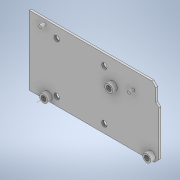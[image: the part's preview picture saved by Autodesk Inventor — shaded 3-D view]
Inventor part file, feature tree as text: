
AUTODESK INVENTOR PART (.ipt)
format: ipt  version: 2021 (Build 250183000, 183)  size: 338,944 bytes
history: native  units: mm
features: reference x23, other x6, sketch x5, plane x2, extrude x2, chamfer x1
ambient origin geometry x8: Origin, YZ Plane, XZ Plane, XY Plane, X Axis, Y Axis, Z Axis, Center Point
bodies: Volumenkörper1 (feature_tree)
feature tree (39):
  plane  "Arbeitsebene1"
  extrude  "Extrusion1"  Depth=4.0mm
  extrude  "Extrusion2"  Depth=3.1505mm
  plane  "Arbeitsebene2"
  chamfer  "Fase1"  Distance=0.1mm
  sketch  "Skizze4"  dims[d6=0.1mm d7=0.1mm d8=0.1mm d9=2.4mm d10=10.0mm d11=8.0mm d12=1.0mm d13=1.0mm d14=1.0mm d15=1.0mm d16=1.0mm d17=1.0mm d18=1.0mm d19=1.0mm d20=1.6mm d21=0.0mm d22=1.64mm d23=1.64mm d24=1.64mm d25=3.6mm d26=0.0mm d27=60.0deg d28=3.8mm d29=0.6mm d30=3.1505mm d31=0.32475mm d32=0.06495mm d33=60.0deg d34=3.8mm d35=0.6mm d36=3.1505mm d37=0.5196mm d38=0.6mm d39=5.8mm d40=10.0mm d41=0.0mm d42=90.0deg d43=90.0deg d44=0.0mm d45=0.0mm d46=0.4mm d47=2.0mm d48=45.0deg d49=0.5mm d50=0.872665mm d51=0.5mm d52=0.872665mm]
  other  "Spirale1"
  sketch  "Skizzenbasierte Anordnung1"  dims[d0=2.4mm d1=4.0mm]
  sketch  "Skizze1"  dims[d2=3.1505mm d3=3.1505mm]
  reference  "Referenz1"
  reference  "Referenz2"
  reference  "Referenz3"
  reference  "Referenz4"
  reference  "Referenz5"
  reference  "Referenz6"
  reference  "Referenz7"
  reference  "Referenz8"
  reference  "Referenz9"
  reference  "Referenz10"
  reference  "Referenz11"
  reference  "Referenz12"
  reference  "Referenz13"
  reference  "Referenz14"
  reference  "Referenz15"
  reference  "Referenz16"
  reference  "Referenz17"
  reference  "Referenz18"
  reference  "Referenz19"
  reference  "Referenz20"
  reference  "Referenz21"
  reference  "Referenz22"
  reference  "Referenz23"
  sketch  "Skizze2"  dims[d4=3.1505mm]
  other  "Arbeitsachse1"
  sketch  "Skizze3"  dims[d5=0.1mm]
  other  "<userpath>\Desktop\Bachelorarbeit\CAD\00_RobotAssembly.iam"
  other  "00_RobotAssembly.iam"
  other  "01_CaseBottom:1"
  other  "arduinoMegaSimplified:1"
